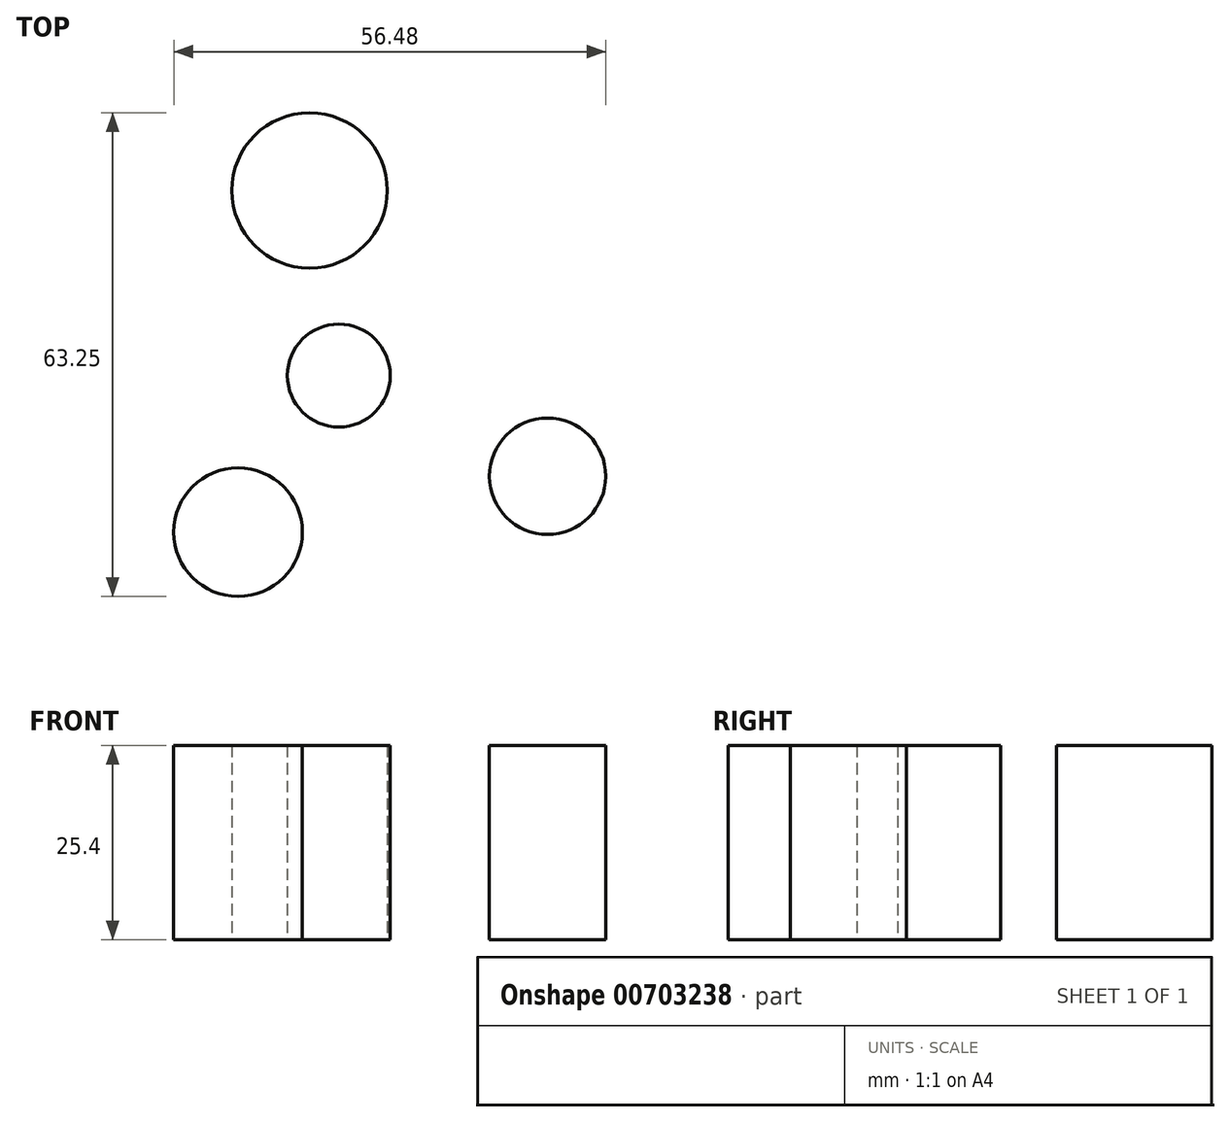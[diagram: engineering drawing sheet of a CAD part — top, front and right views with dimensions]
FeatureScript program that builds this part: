
annotation { "Feature Type Name" : "Feature", "Feature Type Description" : "" }
export const myFeature = defineFeature(function(context is Context, id is Id, definition is map)
    precondition{}
    {
        {
            var Q0;
            Q0=qCreatedBy(makeId("Top.planeOp"),FACE);
            var sketch = newSketch(context, id + "F0", { "sketchPlane" : qUnion([Q0])});
            skArc(sketch, "E0", {"start": v(8.29, 12.17) * mm, "mid": v(17.42, -7.98) * mm, "end": v(36.52, -19.16) * mm});
            skArc(sketch, "E1", {"start": v(21.6, -42.8) * mm, "mid": v(8.13, -43.29) * mm, "end": v(-3.53, -50.03) * mm});
            skArc(sketch, "E2", {"start": v(8.29, 12.17) * mm, "mid": v(-4, 20.9) * mm, "end": v(-11.45, 7.81) * mm});
            skArc(sketch, "E3", {"start": v(8.29, 12.17) * mm, "mid": v(7.1, 10.33) * mm, "end": v(5.07, 11.14) * mm});
            skArc(sketch, "E4", {"start": v(8.29, 12.17) * mm, "mid": v(-8.19, 3.08) * mm, "end": v(-2.75, 21.1) * mm});
            skSolve(sketch);
        }
        {
            var Q0;
            Q0=qCreatedBy(makeId("Top.planeOp"),FACE);
            var sketch = newSketch(context, id + "F1", { "sketchPlane" : qUnion([Q0])});
            skCircle(sketch, "E5", {"center": v(-11.15, -33.7) * mm, "radius": 8.41 * mm});
            skSolve(sketch);
        }
        {
            var Q0;
            Q0=qCreatedBy(makeId("Top.planeOp"),FACE);
            var sketch = newSketch(context, id + "F2", { "sketchPlane" : qUnion([Q0])});
            skCircle(sketch, "E6", {"center": v(29.3, -26.4) * mm, "radius": 7.6 * mm});
            skSolve(sketch);
        }
        {
            var Q0;
            Q0=qCreatedBy(makeId("Top.planeOp"),FACE);
            var sketch = newSketch(context, id + "F3", { "sketchPlane" : qUnion([Q0])});
            skArc(sketch, "E7", {"start": v(-18.14, -29.13) * mm, "mid": v(-9, -11.5) * mm, "end": v(-11.59, 8.17) * mm});
            skArc(sketch, "E8", {"start": v(8.32, 12.13) * mm, "mid": v(12.83, -7.2) * mm, "end": v(28.58, -19.27) * mm});
            skArc(sketch, "E9", {"start": v(25.66, -32.95) * mm, "mid": v(8.64, -29.67) * mm, "end": v(-5.39, -39.84) * mm});
            skSolve(sketch);
        }
        {
            var Q0;
            Q0=qCreatedBy(makeId("Top.planeOp"),FACE);
            var sketch = newSketch(context, id + "F4", { "sketchPlane" : qUnion([Q0])});
            skCircle(sketch, "E10", {"center": v(2.02, -13.23) * mm, "radius": 6.73 * mm});
            skSolve(sketch);
        }
        {
            var Q0;
            {var subQ0=sQuery(id+"F0.wireOp",EDGE,"E2");Q0=makeQuery(id+"F0.imprint","IMPRINT",FACE,{"disambiguationData":[TD([[makeQuery(id+"F0.imprint","IMPRINT",EDGE,{"derivedFrom":subQ0}),1.0]])]});}
            var Q1;
            Q1=makeQuery(id+"F4.imprint","IMPRINT",FACE,{"disambiguationData":[TD([[makeQuery(id+"F4.imprint","IMPRINT",EDGE,{"derivedFrom":sQuery(id+"F4.wireOp",EDGE,"E10")}),1.0]])]});
            var Q2;
            Q2=makeQuery(id+"F1.imprint","IMPRINT",FACE,{"disambiguationData":[TD([[makeQuery(id+"F1.imprint","IMPRINT",EDGE,{"derivedFrom":sQuery(id+"F1.wireOp",EDGE,"E5")}),1.0]])]});
            var Q3;
            Q3=makeQuery(id+"F2.imprint","IMPRINT",FACE,{"disambiguationData":[TD([[makeQuery(id+"F2.imprint","IMPRINT",EDGE,{"derivedFrom":sQuery(id+"F2.wireOp",EDGE,"E6")}),1.0]])]});
            extrude(context, id + "F5", {"entities" : qUnion([Q0, Q1, Q2, Q3]), "depth" : 25.4 * mm, "offsetDistance" : 25.4 * mm});
        }
        {
            var Q0;
            Q0=sQuery(id+"F3.wireOp",EDGE,"E9");
            var Q1;
            Q1=sQuery(id+"F3.wireOp",EDGE,"E7");
            var Q2;
            Q2=sQuery(id+"F3.wireOp",EDGE,"E8");
            extrude(context, id + "F6", {"bodyType" : ToolBodyType.SURFACE, "surfaceEntities" : qUnion([Q0, Q1, Q2]), "depth" : 25.4 * mm, "offsetDistance" : 25.4 * mm});
        }
    });
